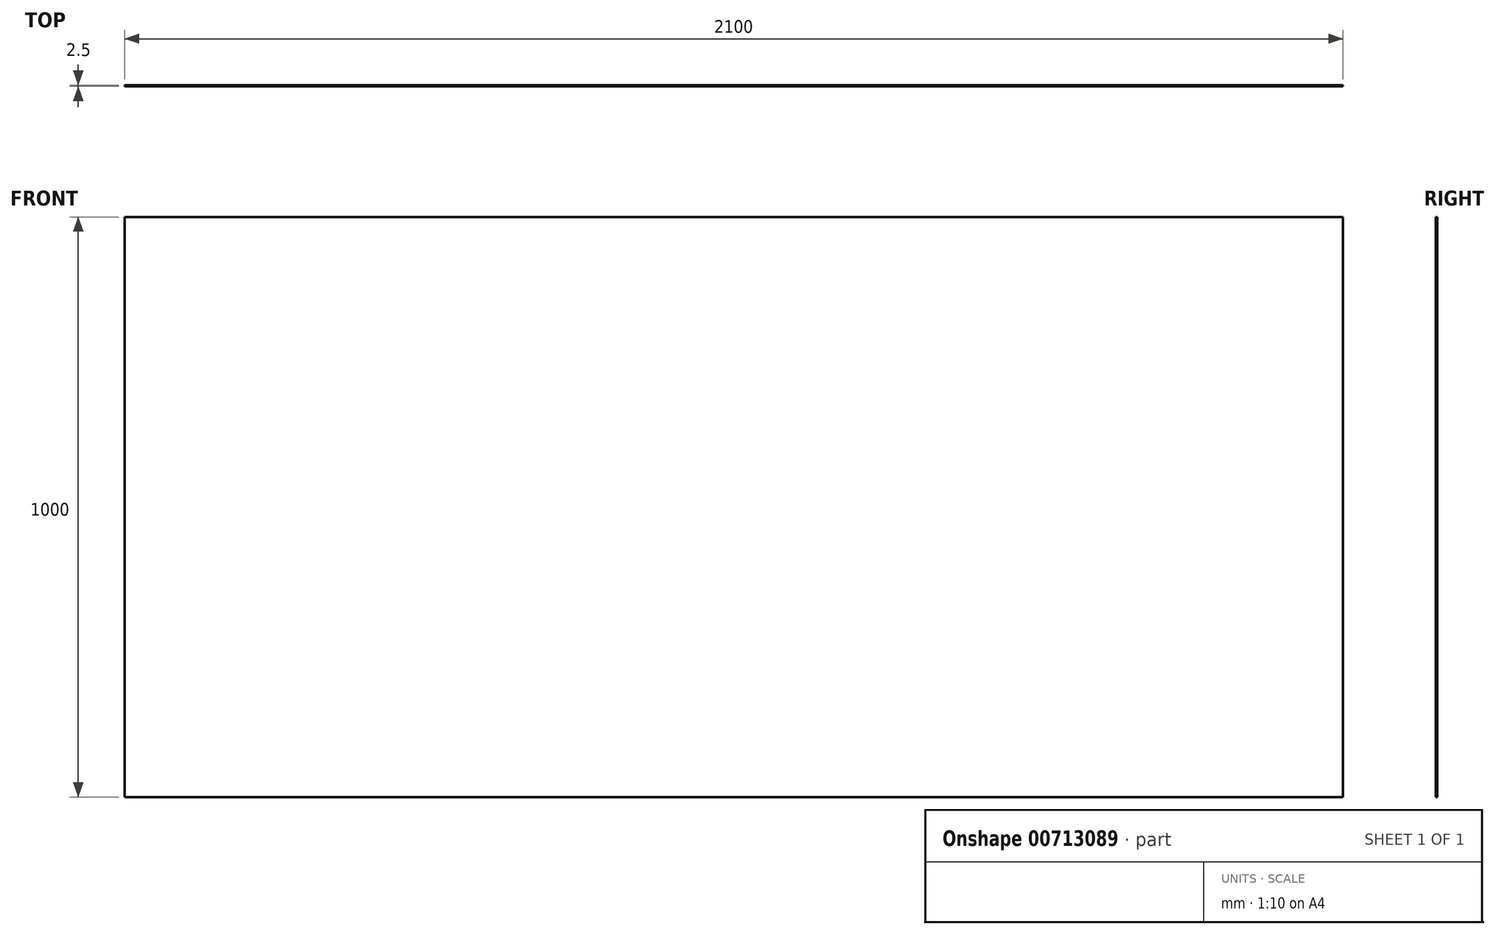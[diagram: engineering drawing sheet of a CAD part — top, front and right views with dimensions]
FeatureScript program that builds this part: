
annotation { "Feature Type Name" : "Feature", "Feature Type Description" : "" }
export const myFeature = defineFeature(function(context is Context, id is Id, definition is map)
    precondition{}
    {
        {
            var Q0;
            Q0=qCreatedBy(makeId("Front.planeOp"),FACE);
            var sketch = newSketch(context, id + "F0", { "sketchPlane" : qUnion([Q0])});
            skLineSegment(sketch, "E0.bottom", {"start": v(0, 0) * mm, "end": v(2100, 0) * mm});
            skLineSegment(sketch, "E0.top", {"start": v(0, 1000) * mm, "end": v(2100, 1000) * mm});
            skLineSegment(sketch, "E0.left", {"start": v(0, 0) * mm, "end": v(0, 1000) * mm});
            skLineSegment(sketch, "E0.right", {"start": v(2100, 0) * mm, "end": v(2100, 1000) * mm});
            skSolve(sketch);
        }
        {
            var Q0;
            Q0=makeQuery(id+"F0.imprint","IMPRINT",FACE,{"disambiguationData":[TD([[makeQuery(id+"F0.imprint","IMPRINT",EDGE,{"derivedFrom":sQuery(id+"F0.wireOp",EDGE,"E0.bottom")}),1.0]])]});
            extrude(context, id + "F1", {"entities" : qUnion([Q0]), "depth" : 2.5 * mm, "offsetDistance" : 25 * mm});
        }
    });
